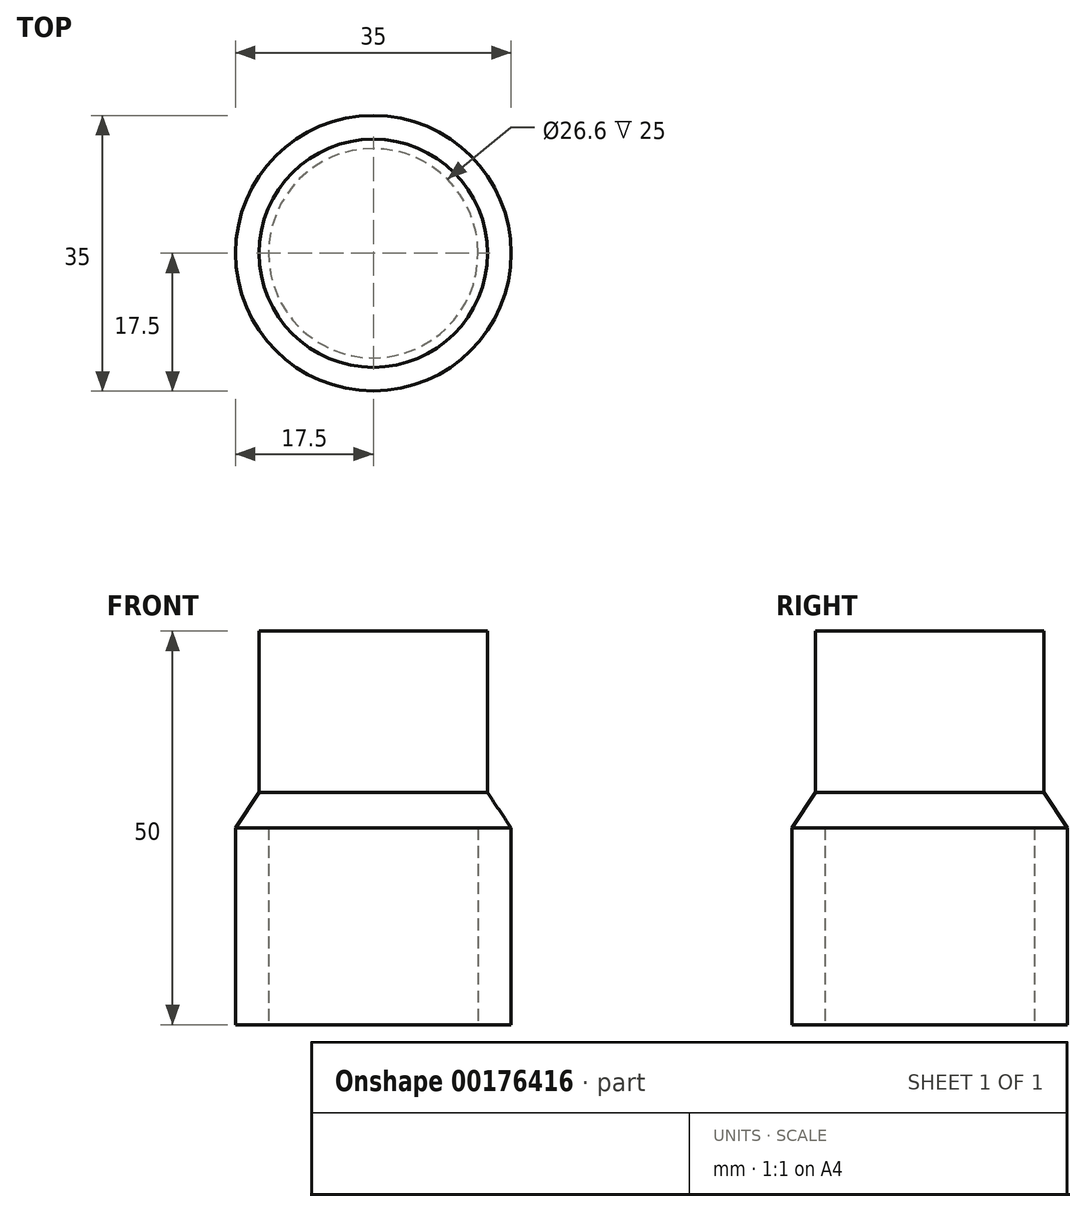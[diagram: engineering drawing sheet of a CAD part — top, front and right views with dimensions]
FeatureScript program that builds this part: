
annotation { "Feature Type Name" : "Feature", "Feature Type Description" : "" }
export const myFeature = defineFeature(function(context is Context, id is Id, definition is map)
    precondition{}
    {
        {
            var Q0;
            Q0=qCreatedBy(makeId("Top.planeOp"),FACE);
            var sketch = newSketch(context, id + "F0", { "sketchPlane" : qUnion([Q0])});
            skCircle(sketch, "E0", {"center": v(0, 0) * mm, "radius": 17.5 * mm});
            skSolve(sketch);
        }
        {
            var Q0;
            Q0=makeQuery(id+"F0.imprint","IMPRINT",FACE,{"disambiguationData":[TD([[makeQuery(id+"F0.imprint","IMPRINT",EDGE,{"derivedFrom":sQuery(id+"F0.wireOp",EDGE,"E0")}),1.0]])]});
            extrude(context, id + "F1", {"entities" : qUnion([Q0]), "depth" : 25 * mm});
        }
        {
            var Q0;
            Q0=makeQuery(id+"F1.opExtrude","CAP_FACE",FACE,{"disambiguationData":[OSD([sQuery(id+"F0.wireOp",EDGE,"E0")])],"isStart":false});
            cPlane(context, id + "F2", {"entities" : qUnion([Q0]), "cplaneType" : CPlaneType.OFFSET, "offset" : 4.5 * mm, "width" : 150 * mm, "height" : 150 * mm});
        }
        {
            var Q0;
            Q0=qCreatedBy(id+"F2.planeOp",FACE);
            var sketch = newSketch(context, id + "F3", { "sketchPlane" : qUnion([Q0])});
            skCircle(sketch, "E1", {"center": v(0, 0) * mm, "radius": 14.5 * mm});
            skSolve(sketch);
        }
        {
            var Q0;
            Q0 = qSketchRegion(id + "F3", true);
            extrude(context, id + "F4", {"entities" : qUnion([Q0]), "depth" : 20.5 * mm});
        }
        {
            var Q0;
            Q0=makeQuery(id+"F1.opExtrude","CAP_FACE",FACE,{"disambiguationData":[OSD([sQuery(id+"F0.wireOp",EDGE,"E0")])],"isStart":false});
            var Q1;
            Q1=makeQuery(id+"F4.opExtrude","CAP_FACE",FACE,{"disambiguationData":[OSD([sQuery(id+"F3.wireOp",EDGE,"E1")])],"isStart":true});
            loft(context, id + "F5", {"sheetProfilesArray" : [{ "sheetProfileEntities" : qUnion([Q0]) }, { "sheetProfileEntities" : qUnion([Q1]) }]});
        }
        {
            var Q0;
            Q0=makeQuery(id+"F4.opExtrude","CAP_FACE",FACE,{"disambiguationData":[OSD([sQuery(id+"F3.wireOp",EDGE,"E1")])],"isStart":false});
            var sketch = newSketch(context, id + "F6", { "sketchPlane" : qUnion([Q0])});
            skPoint(sketch, "E2", {"position": v(0, 0) * mm});
            skSolve(sketch);
        }
        {
            var Q0;
            Q0=sQuery(id+"F6.wireOp",VERTEX,"E2");
            var Q1;
            Q1=makeQuery(id+"F1.opExtrude","SWEPT_BODY",BODY,{"disambiguationData":[OSD([sQuery(id+"F0.wireOp",EDGE,"E0")])]});
            hole(context, id + "F7", {"style" : HoleStyle.SIMPLE, "endStyle" : HoleEndStyle.THROUGH, "holeDiameter" : 25 * mm, "locations" : qUnion([Q0]), "scope" : qUnion([Q1]), "isTappedThrough" : true});
        }
        {
            var Q0;
            Q0=makeQuery(id+"F1.opExtrude","CAP_FACE",FACE,{"disambiguationData":[OSD([sQuery(id+"F0.wireOp",EDGE,"E0")])],"isStart":true});
            var sketch = newSketch(context, id + "F8", { "sketchPlane" : qUnion([Q0])});
            skPoint(sketch, "E3", {"position": v(0, 0) * mm});
            skSolve(sketch);
        }
        {
            var Q0;
            Q0=sQuery(id+"F8.wireOp",VERTEX,"E3");
            var Q1;
            Q1=makeQuery(id+"F1.opExtrude","SWEPT_BODY",BODY,{"disambiguationData":[OSD([sQuery(id+"F0.wireOp",EDGE,"E0")])]});
            hole(context, id + "F9", {"style" : HoleStyle.SIMPLE, "endStyle" : HoleEndStyle.BLIND, "holeDiameter" : 26.6 * mm, "holeDepth" : 25 * mm, "locations" : qUnion([Q0]), "scope" : qUnion([Q1])});
        }
    });
